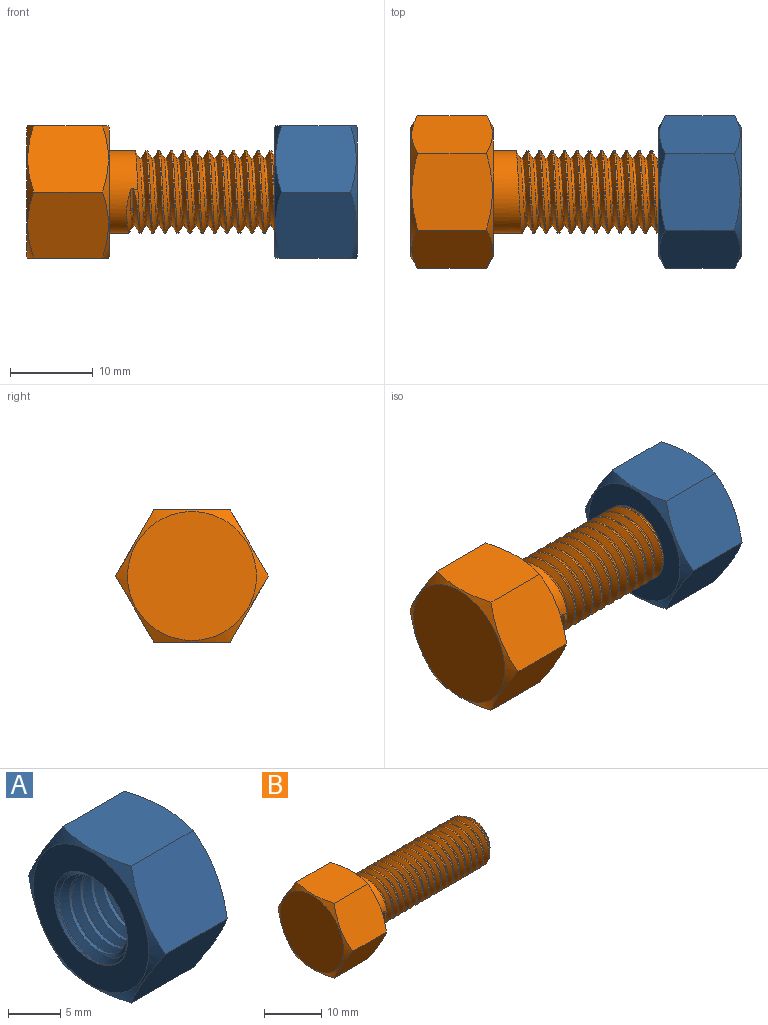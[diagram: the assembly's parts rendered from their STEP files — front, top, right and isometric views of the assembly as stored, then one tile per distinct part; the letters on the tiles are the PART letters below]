
ASSEMBLY  parts=2 mates=1
PART A: 16 faces, bbox 11.2x18.5x18.5 mm
  f0: plane 15.64x15.64mm, normal (1,0,0), area 114.5mm2, adj f4,f5,f6,f7,f9
  f1: plane 15.64x15.64mm, normal (-1,0,0), area 114.5mm2, adj f3,f5,f6,f7,f8
  f2: cylinder r=4.13mm len=8.4mm, axis (-1,0,0), area 54.6mm2, adj f3,f4,f6,f7
  f3: cone r=4.93mm half-angle=45deg, axis (-1,0,0), area 18.2mm2, adj f1,f2,f6,f7
  f4: cone r=4.13mm half-angle=45deg, axis (1,0,0), area 18.2mm2, adj f0,f2,f6,f7
  f5: bspline ~11.61x10.69mm, area 47.7mm2, adj f0,f1,f6,f7
  f6: bspline ~11.42x10.72mm, area 166.2mm2, adj f0,f1,f2,f3,f4,f5
  f7: bspline ~11.42x10.72mm, area 164.8mm2, adj f0,f1,f2,f3,f4,f5
  f8: cone r=7.8mm half-angle=60deg, axis (1,0,0), area 35.3mm2, adj f1,f10,f11,f12,f13,f14,f15
  f9: cone r=10.67mm half-angle=60deg, axis (-1,0,0), area 35.3mm2, adj f0,f10,f11,f12,f13,f14,f15
  f10: plane 9.78x8mm, normal (0,0.87,-0.5), area 85.7mm2, adj f8,f9,f11,f15
  f11: plane 9.77x9.24mm, normal (0,0,-1), area 85.7mm2, adj f8,f9,f10,f12
  f12: plane 9.78x8mm, normal (0,-0.87,-0.5), area 85.7mm2, adj f8,f9,f11,f13
  f13: plane 9.78x8mm, normal (0,-0.87,0.5), area 85.7mm2, adj f8,f9,f12,f14
  f14: plane 9.77x9.24mm, normal (0,0,1), area 85.7mm2, adj f8,f9,f13,f15
  f15: plane 9.78x8mm, normal (0,0.87,0.5), area 85.7mm2, adj f8,f9,f10,f14
PART B: 37 faces, bbox 40.7x18.7x18.7 mm
  f0: plane 15.6x15.6mm, normal (1,0,0), area 112.6mm2, adj f19,f28
  f1: cylinder r=5mm len=4.26mm, axis (-1,0,0), area 0.5mm2, adj f2,f21,f22,f24
  f2: cylinder r=5mm len=10mm, axis (-1,0,0), area 5.9mm2, adj f1,f3,f22,f24
  f3: cylinder r=5mm len=10mm, axis (-1,0,0), area 5.9mm2, adj f2,f4,f22,f24
  f4: cylinder r=5mm len=10mm, axis (-1,0,0), area 5.9mm2, adj f3,f5,f22,f24
  f5: cylinder r=5mm len=10mm, axis (-1,0,0), area 5.9mm2, adj f4,f6,f22,f24
  f6: cylinder r=5mm len=10mm, axis (-1,0,0), area 5.9mm2, adj f5,f7,f22,f24
  f7: cylinder r=5mm len=10mm, axis (-1,0,0), area 5.9mm2, adj f6,f8,f22,f24
  f8: cylinder r=5mm len=10mm, axis (-1,0,0), area 5.9mm2, adj f7,f9,f22,f24
  f9: cylinder r=5mm len=10mm, axis (-1,0,0), area 5.9mm2, adj f8,f10,f22,f24
  f10: cylinder r=5mm len=10mm, axis (-1,0,0), area 5.9mm2, adj f9,f11,f22,f24
  f11: cylinder r=5mm len=10mm, axis (-1,0,0), area 5.9mm2, adj f10,f12,f22,f24
  f12: cylinder r=5mm len=10mm, axis (-1,0,0), area 5.9mm2, adj f11,f13,f22,f24
  f13: cylinder r=5mm len=10mm, axis (-1,0,0), area 5.9mm2, adj f12,f14,f22,f24
  f14: cylinder r=5mm len=10mm, axis (-1,0,0), area 5.9mm2, adj f13,f15,f22,f24
  f15: cylinder r=5mm len=10mm, axis (-1,0,0), area 5.9mm2, adj f14,f16,f22,f24
  f16: cylinder r=5mm len=10mm, axis (-1,0,0), area 5.9mm2, adj f15,f17,f22,f24
  f17: cylinder r=5mm len=10mm, axis (-1,0,0), area 5.9mm2, adj f16,f18,f22,f24
  f18: cylinder r=5mm len=10mm, axis (-1,0,0), area 6.1mm2, adj f17,f19,f22,f24,f27
  f19: cylinder r=5mm len=10mm, axis (-1,0,0), area 85.8mm2, adj f0,f18,f24,f25,f26
  f20: plane 8x8mm, normal (1,0,0), area 50.3mm2, adj f21
  f21: cone r=4mm half-angle=45deg, axis (-1,0,0), area 20.4mm2, adj f1,f20,f22,f23,f24
  f22: bspline ~27.72x11.55mm, area 472.6mm2, adj f1,f2,f3,f4,f5,f6,f7,f8
  f23: bspline ~28.13x9.67mm, area 212.2mm2, adj f21,f22,f24,f26
  f24: bspline ~27.97x11.55mm, area 488.9mm2, adj f1,f2,f3,f4,f5,f6,f7,f8
  f25: plane 3x1.6mm, normal (0.87,-0.43,-0.25), area 1.7mm2, adj f19,f24,f26
  f26: cylinder r=0.22mm len=2.42mm, axis (0,0.5,-0.87), area 1.2mm2, adj f19,f23,f25,f27
  f27: plane 2.77x1.37mm, normal (-0.87,-0.43,-0.25), area 1.7mm2, adj f18,f22,f26
  f28: cone r=10.36mm half-angle=60deg, axis (-1,0,0), area 35.3mm2, adj f0,f29,f30,f31,f32,f33,f34
  f29: plane 9.78x8mm, normal (0,0.87,-0.5), area 85.7mm2, adj f28,f30,f34,f35
  f30: plane 9.77x9.24mm, normal (0,0,-1), area 85.7mm2, adj f28,f29,f31,f35
  f31: plane 9.78x8mm, normal (0,-0.87,-0.5), area 85.7mm2, adj f28,f30,f32,f35
  f32: plane 9.78x8mm, normal (0,-0.87,0.5), area 85.7mm2, adj f28,f31,f33,f35
  f33: plane 9.77x9.24mm, normal (0,0,1), area 85.7mm2, adj f28,f32,f34,f35
  f34: plane 9.78x8mm, normal (0,0.87,0.5), area 85.7mm2, adj f28,f29,f33,f35
  f35: cone r=10.36mm half-angle=60deg, axis (1,0,0), area 35.3mm2, adj f29,f30,f31,f32,f33,f34,f36
  f36: plane 15.6x15.6mm, normal (-1,0,0), area 191.1mm2, adj f35
PLACE A rot(axis=(1,0,0),0.2deg) t=(-10,0,0)mm
PLACE B t=(-40,0,0)mm
MATE cylindrical B.f1 <-> A.f2  axis (1,0,0) through (0,0,0)mm
